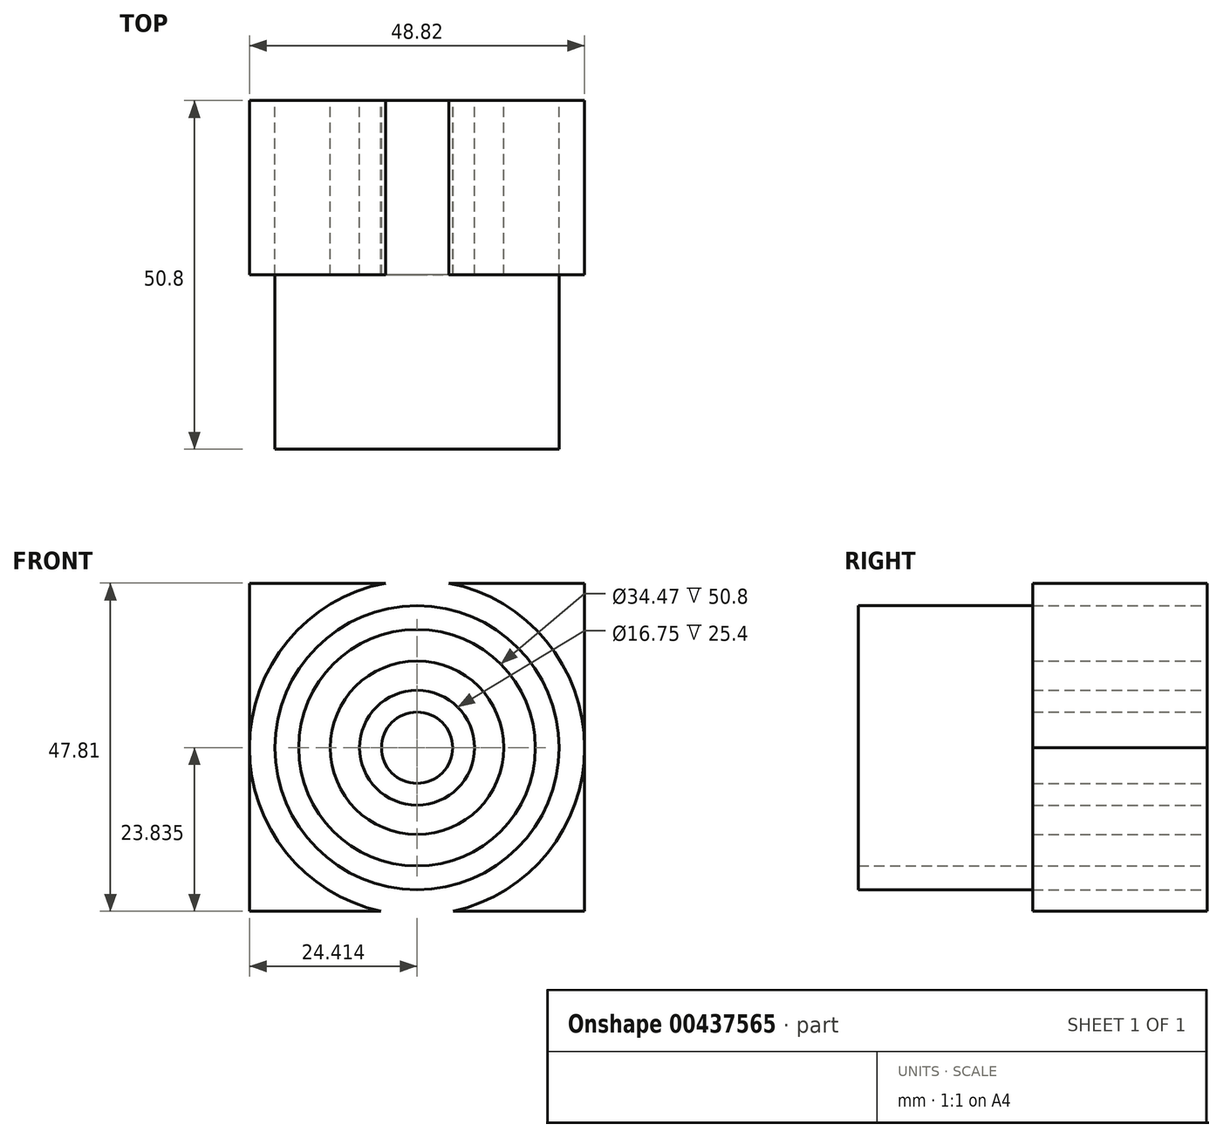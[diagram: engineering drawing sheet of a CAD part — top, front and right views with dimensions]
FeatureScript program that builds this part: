
annotation { "Feature Type Name" : "Feature", "Feature Type Description" : "" }
export const myFeature = defineFeature(function(context is Context, id is Id, definition is map)
    precondition{}
    {
        {
            var Q0;
            Q0=qCreatedBy(makeId("Front.planeOp"),FACE);
            var sketch = newSketch(context, id + "F0", { "sketchPlane" : qUnion([Q0])});
            skLineSegment(sketch, "E0", {"start": v(-32.72, 24.44) * mm, "end": v(-32.72, -23.37) * mm});
            skLineSegment(sketch, "E1", {"start": v(-32.72, 24.44) * mm, "end": v(16.1, 24.44) * mm});
            skLineSegment(sketch, "E2", {"start": v(16.1, 24.44) * mm, "end": v(16.1, -23.37) * mm});
            skLineSegment(sketch, "E3", {"start": v(-32.72, -23.37) * mm, "end": v(16.1, -23.37) * mm});
            skCircle(sketch, "E4", {"center": v(-8.3, 0.47) * mm, "radius": 24.41 * mm});
            skCircle(sketch, "E5", {"center": v(-8.3, 0.47) * mm, "radius": 17.23 * mm});
            skCircle(sketch, "E6", {"center": v(-8.3, 0.47) * mm, "radius": 12.64 * mm});
            skCircle(sketch, "E7", {"center": v(-8.3, 0.47) * mm, "radius": 8.37 * mm});
            skCircle(sketch, "E8", {"center": v(-8.3, 0.47) * mm, "radius": 5.18 * mm});
            skCircle(sketch, "E9", {"center": v(-8.3, 0.47) * mm, "radius": 20.7 * mm});
            skSolve(sketch);
        }
        {
            var Q0;
            {var subQ0=sQuery(id+"F0.wireOp",EDGE,"E1");var subQ1=sQuery(id+"F0.wireOp",EDGE,"E0");var subQ2=makeQuery(id+"F0.imprint","INTERSECT",VERTEX,{"derivedFrom":[subQ1,subQ0]});Q0=makeQuery(id+"F0.imprint","IMPRINT",FACE,{"disambiguationData":[TD([[makeQuery(id+"F0.imprint","IMPRINT",EDGE,{"disambiguationData":[TD([[subQ2,-1.0]])],"derivedFrom":subQ1}),1.0]])]});}
            var Q1;
            {var subQ0=sQuery(id+"F0.wireOp",EDGE,"E3");var subQ1=sQuery(id+"F0.wireOp",EDGE,"E0");var subQ2=makeQuery(id+"F0.imprint","INTERSECT",VERTEX,{"derivedFrom":[subQ1,subQ0]});Q1=makeQuery(id+"F0.imprint","IMPRINT",FACE,{"disambiguationData":[TD([[makeQuery(id+"F0.imprint","IMPRINT",EDGE,{"disambiguationData":[TD([[subQ2,1.0]])],"derivedFrom":subQ1}),1.0]])]});}
            var Q2;
            {var subQ0=sQuery(id+"F0.wireOp",EDGE,"E4");var subQ1=sQuery(id+"F0.wireOp",EDGE,"E1");var subQ2=makeQuery(id+"F0.imprint","INTERSECT",VERTEX,{"disambiguationData":[OD(0.0)],"derivedFrom":[subQ1,subQ0]});Q2=makeQuery(id+"F0.imprint","IMPRINT",FACE,{"disambiguationData":[TD([[makeQuery(id+"F0.imprint","IMPRINT",EDGE,{"disambiguationData":[TD([[subQ2,-1.0]])],"derivedFrom":subQ1}),1.0]])]});}
            var Q3;
            {var subQ0=sQuery(id+"F0.wireOp",EDGE,"E2");var subQ1=sQuery(id+"F0.wireOp",EDGE,"E1");var subQ2=makeQuery(id+"F0.imprint","INTERSECT",VERTEX,{"derivedFrom":[subQ1,subQ0]});Q3=makeQuery(id+"F0.imprint","IMPRINT",FACE,{"disambiguationData":[TD([[makeQuery(id+"F0.imprint","IMPRINT",EDGE,{"disambiguationData":[TD([[subQ2,1.0]])],"derivedFrom":subQ1}),-1.0]])]});}
            var Q4;
            {var subQ0=sQuery(id+"F0.wireOp",EDGE,"E3");var subQ1=sQuery(id+"F0.wireOp",EDGE,"E2");var subQ2=makeQuery(id+"F0.imprint","INTERSECT",VERTEX,{"derivedFrom":[subQ1,subQ0]});Q4=makeQuery(id+"F0.imprint","IMPRINT",FACE,{"disambiguationData":[TD([[makeQuery(id+"F0.imprint","IMPRINT",EDGE,{"disambiguationData":[TD([[subQ2,1.0]])],"derivedFrom":subQ1}),-1.0]])]});}
            var Q5;
            {var subQ0=sQuery(id+"F0.wireOp",EDGE,"E4");var subQ1=sQuery(id+"F0.wireOp",EDGE,"E3");var subQ2=makeQuery(id+"F0.imprint","INTERSECT",VERTEX,{"disambiguationData":[OD(0.0)],"derivedFrom":[subQ1,subQ0]});Q5=makeQuery(id+"F0.imprint","IMPRINT",FACE,{"disambiguationData":[TD([[makeQuery(id+"F0.imprint","IMPRINT",EDGE,{"disambiguationData":[TD([[subQ2,-1.0]])],"derivedFrom":subQ1}),-1.0]])]});}
            var Q6;
            Q6=makeQuery(id+"F0.imprint","IMPRINT",FACE,{"disambiguationData":[TD([[makeQuery(id+"F0.imprint","IMPRINT",EDGE,{"derivedFrom":sQuery(id+"F0.wireOp",EDGE,"xT3kC6Zv-lnp0-rQDq-dMAk-a3f1kGmynLMM")}),1.0]])]});
            var Q7;
            Q7=makeQuery(id+"F0.imprint","IMPRINT",FACE,{"disambiguationData":[TD([[makeQuery(id+"F0.imprint","IMPRINT",EDGE,{"derivedFrom":sQuery(id+"F0.wireOp",EDGE,"E6")}),1.0]])]});
            var Q8;
            Q8=makeQuery(id+"F0.imprint","IMPRINT",FACE,{"disambiguationData":[TD([[makeQuery(id+"F0.imprint","IMPRINT",EDGE,{"derivedFrom":sQuery(id+"F0.wireOp",EDGE,"E8")}),1.0]])]});
            var Q9;
            Q9=makeQuery(id+"F0.imprint","IMPRINT",FACE,{"disambiguationData":[TD([[makeQuery(id+"F0.imprint","IMPRINT",EDGE,{"derivedFrom":sQuery(id+"F0.wireOp",EDGE,"E5")}),-1.0]])]});
            extrude(context, id + "F1", {"entities" : qUnion([Q0, Q1, Q2, Q3, Q4, Q5, Q6, Q7, Q8, Q9]), "depth" : 25.4 * mm});
        }
        {
            var Q0;
            Q0=makeQuery(id+"F1.opExtrude","CAP_FACE",FACE,{"disambiguationData":[OSD([sQuery(id+"F0.wireOp",EDGE,"xT3kC6Zv-lnp0-rQDq-dMAk-a3f1kGmynLMM"),sQuery(id+"F0.wireOp",EDGE,"E5")])],"isStart":false});
            extrude(context, id + "F2", {"entities" : qUnion([Q0]), "operationType" : NewBodyOperationType.ADD, "depth" : 25.4 * mm});
        }
    });
